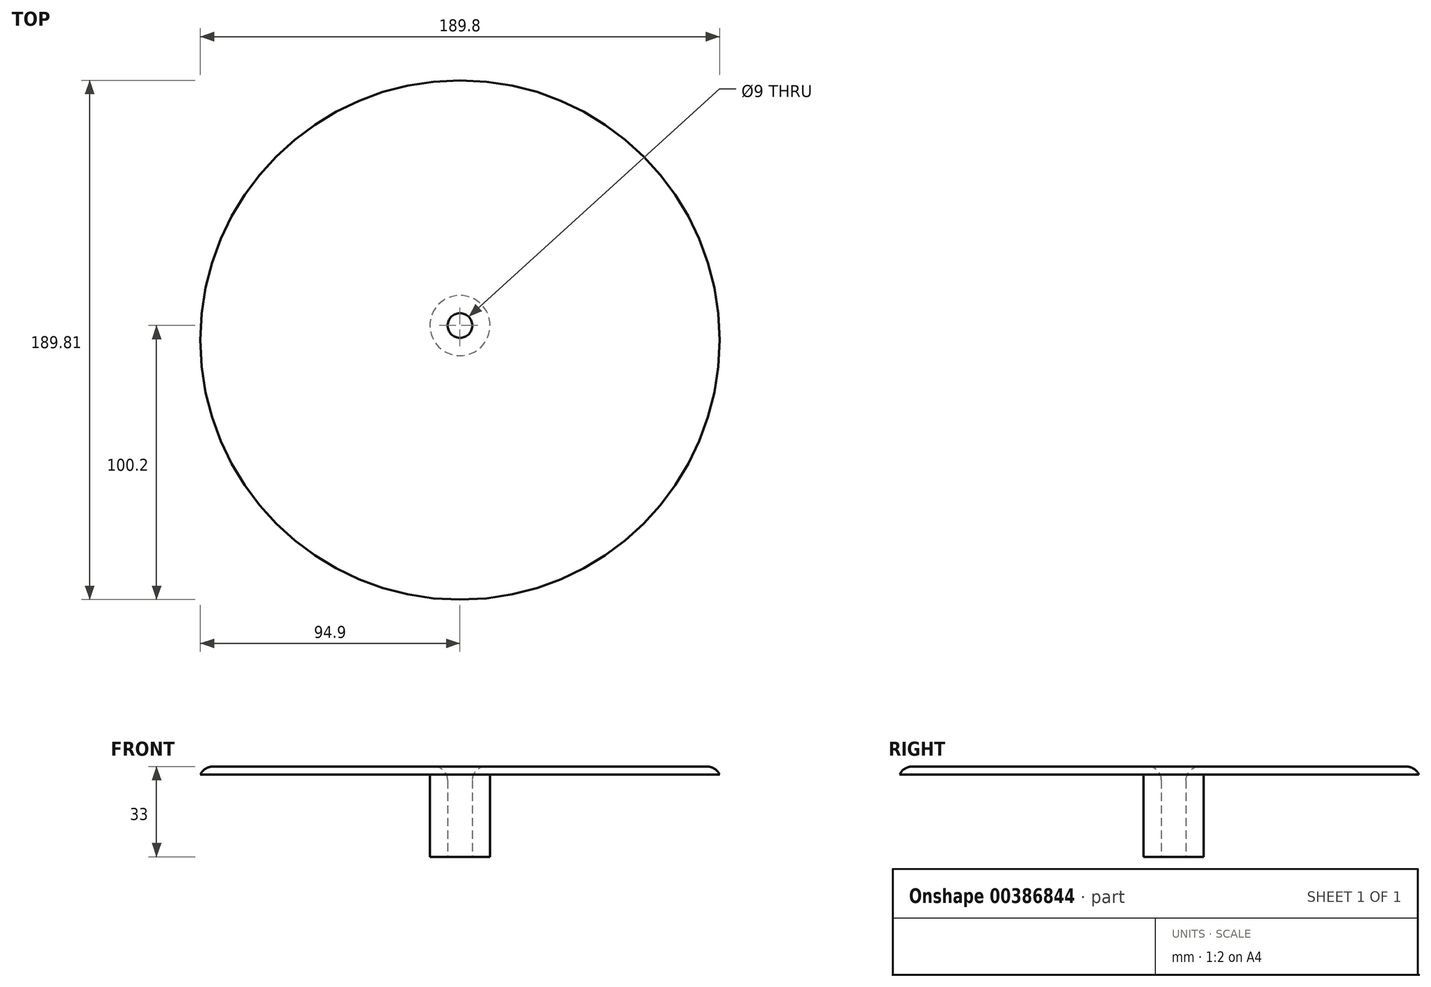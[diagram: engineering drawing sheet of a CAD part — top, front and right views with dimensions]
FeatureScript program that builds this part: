
annotation { "Feature Type Name" : "Feature", "Feature Type Description" : "" }
export const myFeature = defineFeature(function(context is Context, id is Id, definition is map)
    precondition{}
    {
        {
            var Q0;
            Q0=qCreatedBy(makeId("Top.planeOp"),FACE);
            var sketch = newSketch(context, id + "F0", { "sketchPlane" : qUnion([Q0])});
            skCircle(sketch, "E0", {"center": v(0, -5.3) * mm, "radius": 94.9 * mm});
            skCircle(sketch, "E1", {"center": v(0, 0) * mm, "radius": 4.5 * mm});
            skSolve(sketch);
        }
        {
            var Q0;
            Q0 = qSketchRegion(id + "F0", true);
            extrude(context, id + "F1", {"entities" : qUnion([Q0]), "depth" : 3 * mm});
        }
        {
            var Q0;
            Q0=makeQuery(id+"F1.opExtrude","CAP_FACE",FACE,{"disambiguationData":[OSD([sQuery(id+"F0.wireOp",EDGE,"E0"),sQuery(id+"F0.wireOp",EDGE,"E1")])],"isStart":true});
            var sketch = newSketch(context, id + "F2", { "sketchPlane" : qUnion([Q0])});
            skCircle(sketch, "E2", {"center": v(0, 0) * mm, "radius": 11 * mm});
            skCircle(sketch, "E3", {"center": v(0, 0) * mm, "radius": 4.5 * mm});
            skSolve(sketch);
        }
        {
            var Q0;
            Q0 = qSketchRegion(id + "F2", true);
            extrude(context, id + "F3", {"entities" : qUnion([Q0]), "operationType" : NewBodyOperationType.ADD, "depth" : 30 * mm});
        }
        {
            var Q0;
            Q0=makeQuery(id+"F1.opExtrude","CAP_FACE",FACE,{"disambiguationData":[OSD([sQuery(id+"F0.wireOp",EDGE,"E0"),sQuery(id+"F0.wireOp",EDGE,"E1")])],"isStart":false});
            fillet(context, id + "F4", {"entities" : qUnion([Q0]), "radius" : 5 * mm, "tangentPropagation" : true, "allowEdgeOverflow" : false});
        }
    });
